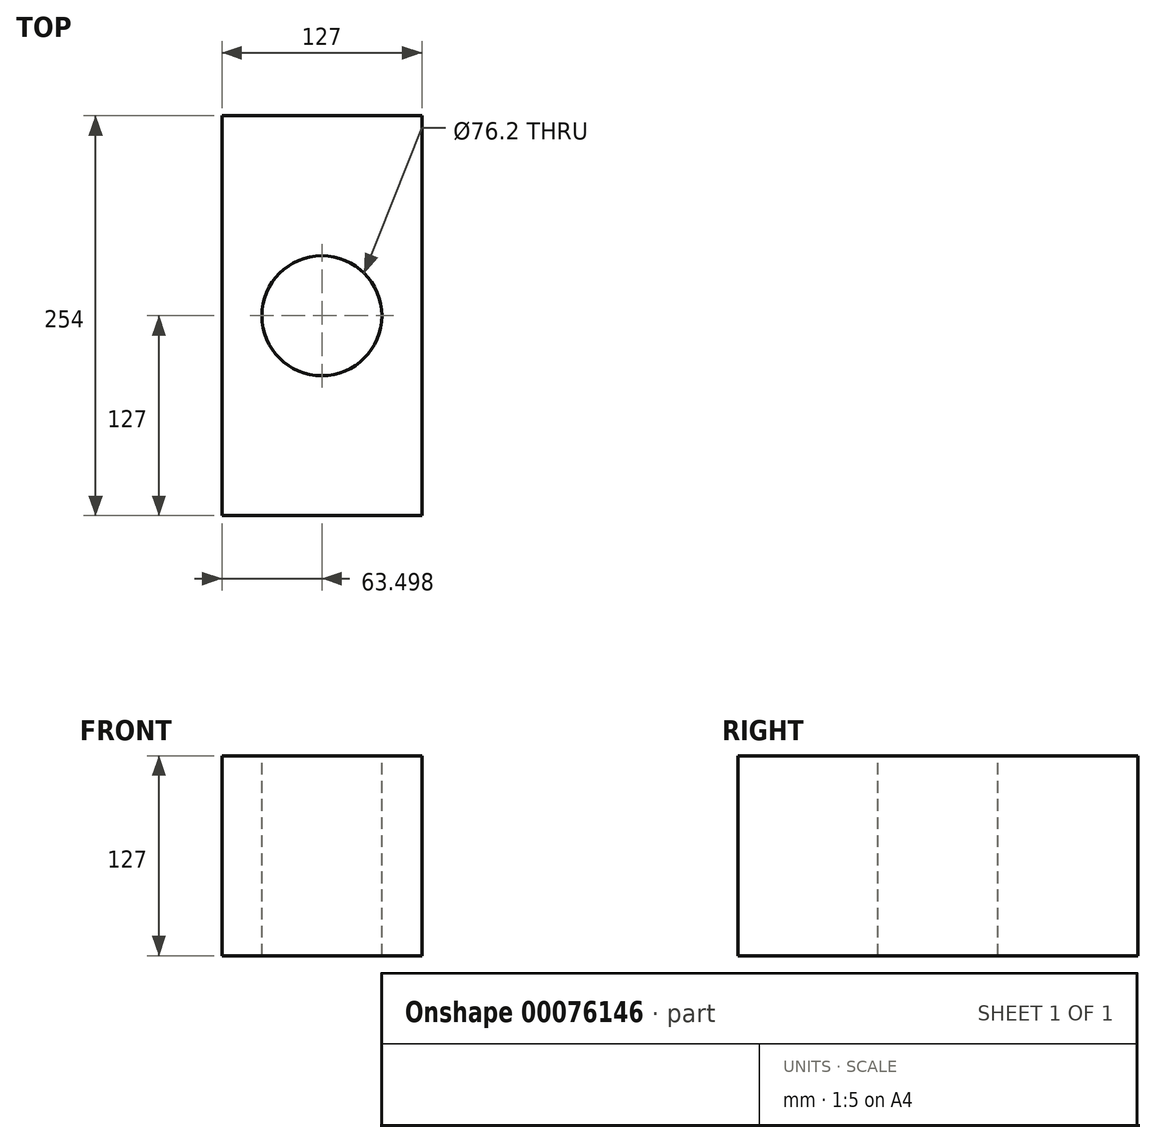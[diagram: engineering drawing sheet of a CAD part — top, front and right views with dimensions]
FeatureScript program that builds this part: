
annotation { "Feature Type Name" : "Feature", "Feature Type Description" : "" }
export const myFeature = defineFeature(function(context is Context, id is Id, definition is map)
    precondition{}
    {
        {
            var Q0;
            Q0=qCreatedBy(makeId("Front.planeOp"),FACE);
            var sketch = newSketch(context, id + "F0", { "sketchPlane" : qUnion([Q0])});
            skLineSegment(sketch, "E0.bottom", {"start": v(-69.54, 65.8) * mm, "end": v(57.46, 65.8) * mm});
            skLineSegment(sketch, "E0.top", {"start": v(-69.54, -61.2) * mm, "end": v(57.46, -61.2) * mm});
            skLineSegment(sketch, "E0.left", {"start": v(-69.54, 65.8) * mm, "end": v(-69.54, -61.2) * mm});
            skLineSegment(sketch, "E0.right", {"start": v(57.46, 65.8) * mm, "end": v(57.46, -61.2) * mm});
            skSolve(sketch);
        }
        {
            var Q0;
            Q0=makeQuery(id+"F0.imprint","IMPRINT",FACE,{"disambiguationData":[TD([[makeQuery(id+"F0.imprint","IMPRINT",EDGE,{"derivedFrom":sQuery(id+"F0.wireOp",EDGE,"E0.bottom")}),-1.0]])]});
            extrude(context, id + "F1", {"entities" : qUnion([Q0]), "depth" : 254 * mm});
        }
        {
            var Q0;
            Q0=makeQuery(id+"F1.opExtrude","SWEPT_FACE",FACE,{"disambiguationData":[OSD([sQuery(id+"F0.wireOp",EDGE,"E0.bottom")])]});
            var sketch = newSketch(context, id + "F2", { "sketchPlane" : qUnion([Q0])});
            skLineSegment(sketch, "E1.bottom", {"start": v(57.46, -254) * mm, "end": v(-6.04, -254) * mm});
            skLineSegment(sketch, "E1.top", {"start": v(57.46, -127) * mm, "end": v(-6.04, -127) * mm});
            skLineSegment(sketch, "E1.left", {"start": v(57.46, -254) * mm, "end": v(57.46, -127) * mm});
            skLineSegment(sketch, "E1.right", {"start": v(-6.04, -254) * mm, "end": v(-6.04, -127) * mm});
            skCircle(sketch, "E2", {"center": v(-6.04, -127) * mm, "radius": 38.1 * mm});
            skSolve(sketch);
        }
        {
            var Q0;
            Q0=sQuery(id+"F2.wireOp",VERTEX,"E1.top.end");
            var Q1;
            Q1=makeQuery(id+"F1.opExtrude","SWEPT_BODY",BODY,{"disambiguationData":[OSD([sQuery(id+"F0.wireOp",EDGE,"E0.bottom"),sQuery(id+"F0.wireOp",EDGE,"E0.top"),sQuery(id+"F0.wireOp",EDGE,"E0.left"),sQuery(id+"F0.wireOp",EDGE,"E0.right")])]});
            hole(context, id + "F3", {"style" : HoleStyle.SIMPLE, "endStyle" : HoleEndStyle.THROUGH, "holeDiameter" : 76.2 * mm, "locations" : qUnion([Q0]), "scope" : qUnion([Q1]), "isTappedThrough" : true});
        }
    });
